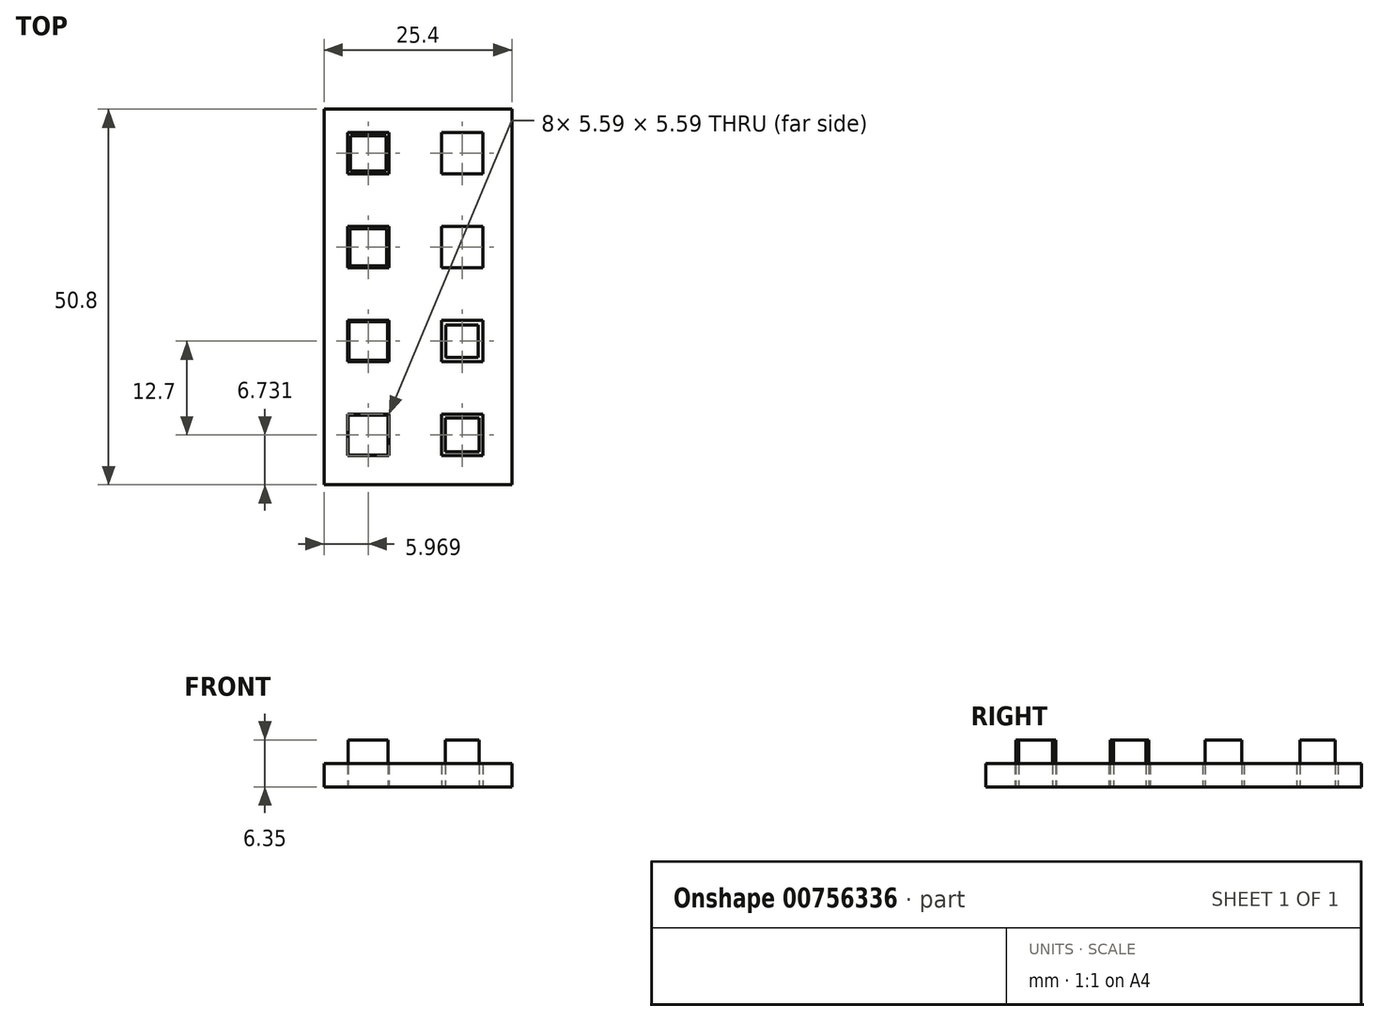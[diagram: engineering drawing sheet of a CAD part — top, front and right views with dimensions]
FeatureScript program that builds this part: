
annotation { "Feature Type Name" : "Feature", "Feature Type Description" : "" }
export const myFeature = defineFeature(function(context is Context, id is Id, definition is map)
    precondition{}
    {
        {
            var Q0;
            Q0=qCreatedBy(makeId("Top.planeOp"),FACE);
            var sketch = newSketch(context, id + "F0", { "sketchPlane" : qUnion([Q0])});
            skLineSegment(sketch, "E0.bottom", {"start": v(0, 0) * mm, "end": v(50.8, 0) * mm});
            skLineSegment(sketch, "E0.top", {"start": v(0, 50.8) * mm, "end": v(50.8, 50.8) * mm});
            skLineSegment(sketch, "E0.left", {"start": v(0, 0) * mm, "end": v(0, 50.8) * mm});
            skLineSegment(sketch, "E0.right", {"start": v(50.8, 0) * mm, "end": v(50.8, 50.8) * mm});
            skLineSegment(sketch, "E1.bottom", {"start": v(3.17, 47.63) * mm, "end": v(8.76, 47.63) * mm});
            skLineSegment(sketch, "E1.top", {"start": v(3.17, 42.04) * mm, "end": v(8.76, 42.04) * mm});
            skLineSegment(sketch, "E1.left", {"start": v(3.17, 47.63) * mm, "end": v(3.17, 42.04) * mm});
            skLineSegment(sketch, "E1.right", {"start": v(8.76, 47.63) * mm, "end": v(8.76, 42.04) * mm});
            skLineSegment(sketch, "E2.0.1.0", {"start": v(3.17, 34.93) * mm, "end": v(8.76, 34.93) * mm});
            skLineSegment(sketch, "E2.0.1.1", {"start": v(3.17, 29.34) * mm, "end": v(8.76, 29.34) * mm});
            skLineSegment(sketch, "E2.0.1.2", {"start": v(8.76, 34.93) * mm, "end": v(8.76, 29.34) * mm});
            skLineSegment(sketch, "E2.0.1.3", {"start": v(3.17, 34.93) * mm, "end": v(3.17, 29.34) * mm});
            skLineSegment(sketch, "E2.0.2.0", {"start": v(3.17, 22.23) * mm, "end": v(8.76, 22.23) * mm});
            skLineSegment(sketch, "E2.0.2.1", {"start": v(3.18, 16.64) * mm, "end": v(8.76, 16.64) * mm});
            skLineSegment(sketch, "E2.0.2.2", {"start": v(8.76, 22.23) * mm, "end": v(8.76, 16.64) * mm});
            skLineSegment(sketch, "E2.0.2.3", {"start": v(3.17, 22.23) * mm, "end": v(3.17, 16.64) * mm});
            skLineSegment(sketch, "E2.0.3.0", {"start": v(3.17, 9.53) * mm, "end": v(8.76, 9.53) * mm});
            skLineSegment(sketch, "E2.0.3.1", {"start": v(3.18, 3.94) * mm, "end": v(8.76, 3.94) * mm});
            skLineSegment(sketch, "E2.0.3.2", {"start": v(8.76, 9.53) * mm, "end": v(8.76, 3.94) * mm});
            skLineSegment(sketch, "E2.0.3.3", {"start": v(3.17, 9.53) * mm, "end": v(3.17, 3.94) * mm});
            skLineSegment(sketch, "E2.1.0.0", {"start": v(15.87, 47.63) * mm, "end": v(21.46, 47.63) * mm});
            skLineSegment(sketch, "E2.1.0.1", {"start": v(15.87, 42.04) * mm, "end": v(21.46, 42.04) * mm});
            skLineSegment(sketch, "E2.1.0.2", {"start": v(21.46, 47.63) * mm, "end": v(21.46, 42.04) * mm});
            skLineSegment(sketch, "E2.1.0.3", {"start": v(15.87, 47.63) * mm, "end": v(15.87, 42.04) * mm});
            skLineSegment(sketch, "E2.1.1.0", {"start": v(15.87, 34.93) * mm, "end": v(21.46, 34.93) * mm});
            skLineSegment(sketch, "E2.1.1.1", {"start": v(15.88, 29.34) * mm, "end": v(21.46, 29.34) * mm});
            skLineSegment(sketch, "E2.1.1.2", {"start": v(21.46, 34.93) * mm, "end": v(21.46, 29.34) * mm});
            skLineSegment(sketch, "E2.1.1.3", {"start": v(15.87, 34.93) * mm, "end": v(15.87, 29.34) * mm});
            skLineSegment(sketch, "E2.1.2.0", {"start": v(15.87, 22.23) * mm, "end": v(21.46, 22.23) * mm});
            skLineSegment(sketch, "E2.1.2.1", {"start": v(15.88, 16.64) * mm, "end": v(21.46, 16.64) * mm});
            skLineSegment(sketch, "E2.1.2.2", {"start": v(21.46, 22.23) * mm, "end": v(21.46, 16.64) * mm});
            skLineSegment(sketch, "E2.1.2.3", {"start": v(15.87, 22.23) * mm, "end": v(15.87, 16.64) * mm});
            skLineSegment(sketch, "E2.1.3.0", {"start": v(15.87, 9.53) * mm, "end": v(21.46, 9.53) * mm});
            skLineSegment(sketch, "E2.1.3.1", {"start": v(15.88, 3.94) * mm, "end": v(21.46, 3.94) * mm});
            skLineSegment(sketch, "E2.1.3.2", {"start": v(21.46, 9.53) * mm, "end": v(21.46, 3.94) * mm});
            skLineSegment(sketch, "E2.1.3.3", {"start": v(15.87, 9.53) * mm, "end": v(15.87, 3.94) * mm});
            skLineSegment(sketch, "E2.2.0.0", {"start": v(28.57, 47.63) * mm, "end": v(34.16, 47.63) * mm});
            skLineSegment(sketch, "E2.2.0.1", {"start": v(28.57, 42.04) * mm, "end": v(34.16, 42.04) * mm});
            skLineSegment(sketch, "E2.2.0.2", {"start": v(34.16, 47.63) * mm, "end": v(34.16, 42.04) * mm});
            skLineSegment(sketch, "E2.2.0.3", {"start": v(28.57, 47.63) * mm, "end": v(28.57, 42.04) * mm});
            skLineSegment(sketch, "E2.2.1.0", {"start": v(28.57, 34.93) * mm, "end": v(34.16, 34.93) * mm});
            skLineSegment(sketch, "E2.2.1.1", {"start": v(28.57, 29.34) * mm, "end": v(34.16, 29.34) * mm});
            skLineSegment(sketch, "E2.2.1.2", {"start": v(34.16, 34.93) * mm, "end": v(34.16, 29.34) * mm});
            skLineSegment(sketch, "E2.2.1.3", {"start": v(28.57, 34.93) * mm, "end": v(28.57, 29.34) * mm});
            skLineSegment(sketch, "E2.2.2.0", {"start": v(28.57, 22.23) * mm, "end": v(34.16, 22.23) * mm});
            skLineSegment(sketch, "E2.2.2.1", {"start": v(28.57, 16.64) * mm, "end": v(34.16, 16.64) * mm});
            skLineSegment(sketch, "E2.2.2.2", {"start": v(34.16, 22.23) * mm, "end": v(34.16, 16.64) * mm});
            skLineSegment(sketch, "E2.2.2.3", {"start": v(28.57, 22.23) * mm, "end": v(28.57, 16.64) * mm});
            skLineSegment(sketch, "E2.2.3.0", {"start": v(28.57, 9.53) * mm, "end": v(34.16, 9.53) * mm});
            skLineSegment(sketch, "E2.2.3.1", {"start": v(28.58, 3.94) * mm, "end": v(34.16, 3.94) * mm});
            skLineSegment(sketch, "E2.2.3.2", {"start": v(34.16, 9.53) * mm, "end": v(34.16, 3.94) * mm});
            skLineSegment(sketch, "E2.2.3.3", {"start": v(28.57, 9.53) * mm, "end": v(28.57, 3.94) * mm});
            skLineSegment(sketch, "E2.3.0.0", {"start": v(41.27, 47.63) * mm, "end": v(46.86, 47.63) * mm});
            skLineSegment(sketch, "E2.3.0.1", {"start": v(41.27, 42.04) * mm, "end": v(46.86, 42.04) * mm});
            skLineSegment(sketch, "E2.3.0.2", {"start": v(46.86, 47.63) * mm, "end": v(46.86, 42.04) * mm});
            skLineSegment(sketch, "E2.3.0.3", {"start": v(41.28, 47.63) * mm, "end": v(41.28, 42.04) * mm});
            skLineSegment(sketch, "E2.3.1.0", {"start": v(41.27, 34.93) * mm, "end": v(46.86, 34.93) * mm});
            skLineSegment(sketch, "E2.3.1.1", {"start": v(41.27, 29.34) * mm, "end": v(46.86, 29.34) * mm});
            skLineSegment(sketch, "E2.3.1.2", {"start": v(46.86, 34.93) * mm, "end": v(46.86, 29.34) * mm});
            skLineSegment(sketch, "E2.3.1.3", {"start": v(41.28, 34.93) * mm, "end": v(41.28, 29.34) * mm});
            skLineSegment(sketch, "E2.3.2.0", {"start": v(41.27, 22.23) * mm, "end": v(46.86, 22.23) * mm});
            skLineSegment(sketch, "E2.3.2.1", {"start": v(41.27, 16.64) * mm, "end": v(46.86, 16.64) * mm});
            skLineSegment(sketch, "E2.3.2.2", {"start": v(46.86, 22.23) * mm, "end": v(46.86, 16.64) * mm});
            skLineSegment(sketch, "E2.3.2.3", {"start": v(41.28, 22.23) * mm, "end": v(41.28, 16.64) * mm});
            skLineSegment(sketch, "E2.3.3.0", {"start": v(41.27, 9.53) * mm, "end": v(46.86, 9.53) * mm});
            skLineSegment(sketch, "E2.3.3.1", {"start": v(41.27, 3.94) * mm, "end": v(46.86, 3.94) * mm});
            skLineSegment(sketch, "E2.3.3.2", {"start": v(46.86, 9.53) * mm, "end": v(46.86, 3.94) * mm});
            skLineSegment(sketch, "E2.3.3.3", {"start": v(41.28, 9.53) * mm, "end": v(41.28, 3.94) * mm});
            skLineSegment(sketch, "E2.direction1", {"start": v(3.17, 42.04) * mm, "end": v(15.87, 42.04) * mm, "construction": true});
            skLineSegment(sketch, "E2.direction2", {"start": v(3.17, 42.04) * mm, "end": v(3.17, 29.34) * mm, "construction": true});
            skSolve(sketch);
        }
        {
            var Q0;
            Q0 = qSketchRegion(id + "F0", true);
            extrude(context, id + "F1", {"entities" : qUnion([Q0]), "depth" : 3.17 * mm, "offsetDistance" : 25.4 * mm});
        }
        {
            var Q0;
            Q0=makeQuery(id+"F1.opExtrude","CAP_FACE",FACE,{"disambiguationData":[OSD([sQuery(id+"F0.wireOp",EDGE,"E0.bottom"),sQuery(id+"F0.wireOp",EDGE,"E0.top"),sQuery(id+"F0.wireOp",EDGE,"E0.left"),sQuery(id+"F0.wireOp",EDGE,"E0.right"),sQuery(id+"F0.wireOp",EDGE,"E1.bottom"),sQuery(id+"F0.wireOp",EDGE,"E1.top"),sQuery(id+"F0.wireOp",EDGE,"E1.left"),sQuery(id+"F0.wireOp",EDGE,"E1.right"),sQuery(id+"F0.wireOp",EDGE,"E2.0.1.0"),sQuery(id+"F0.wireOp",EDGE,"E2.0.1.1"),sQuery(id+"F0.wireOp",EDGE,"E2.0.1.2"),sQuery(id+"F0.wireOp",EDGE,"E2.0.1.3"),sQuery(id+"F0.wireOp",EDGE,"E2.0.2.0"),sQuery(id+"F0.wireOp",EDGE,"E2.0.2.1"),sQuery(id+"F0.wireOp",EDGE,"E2.0.2.2"),sQuery(id+"F0.wireOp",EDGE,"E2.0.2.3"),sQuery(id+"F0.wireOp",EDGE,"E2.0.3.0"),sQuery(id+"F0.wireOp",EDGE,"E2.0.3.1"),sQuery(id+"F0.wireOp",EDGE,"E2.0.3.2"),sQuery(id+"F0.wireOp",EDGE,"E2.0.3.3"),sQuery(id+"F0.wireOp",EDGE,"E2.1.0.0"),sQuery(id+"F0.wireOp",EDGE,"E2.1.0.1"),sQuery(id+"F0.wireOp",EDGE,"E2.1.0.2"),sQuery(id+"F0.wireOp",EDGE,"E2.1.0.3"),sQuery(id+"F0.wireOp",EDGE,"E2.1.1.0"),sQuery(id+"F0.wireOp",EDGE,"E2.1.1.1"),sQuery(id+"F0.wireOp",EDGE,"E2.1.1.2"),sQuery(id+"F0.wireOp",EDGE,"E2.1.1.3"),sQuery(id+"F0.wireOp",EDGE,"E2.1.2.0"),sQuery(id+"F0.wireOp",EDGE,"E2.1.2.1"),sQuery(id+"F0.wireOp",EDGE,"E2.1.2.2"),sQuery(id+"F0.wireOp",EDGE,"E2.1.2.3"),sQuery(id+"F0.wireOp",EDGE,"E2.1.3.0"),sQuery(id+"F0.wireOp",EDGE,"E2.1.3.1"),sQuery(id+"F0.wireOp",EDGE,"E2.1.3.2"),sQuery(id+"F0.wireOp",EDGE,"E2.1.3.3"),sQuery(id+"F0.wireOp",EDGE,"E2.2.0.0"),sQuery(id+"F0.wireOp",EDGE,"E2.2.0.1"),sQuery(id+"F0.wireOp",EDGE,"E2.2.0.2"),sQuery(id+"F0.wireOp",EDGE,"E2.2.0.3"),sQuery(id+"F0.wireOp",EDGE,"E2.2.1.0"),sQuery(id+"F0.wireOp",EDGE,"E2.2.1.1"),sQuery(id+"F0.wireOp",EDGE,"E2.2.1.2"),sQuery(id+"F0.wireOp",EDGE,"E2.2.1.3"),sQuery(id+"F0.wireOp",EDGE,"E2.2.2.0"),sQuery(id+"F0.wireOp",EDGE,"E2.2.2.1"),sQuery(id+"F0.wireOp",EDGE,"E2.2.2.2"),sQuery(id+"F0.wireOp",EDGE,"E2.2.2.3"),sQuery(id+"F0.wireOp",EDGE,"E2.2.3.0"),sQuery(id+"F0.wireOp",EDGE,"E2.2.3.1"),sQuery(id+"F0.wireOp",EDGE,"E2.2.3.2"),sQuery(id+"F0.wireOp",EDGE,"E2.2.3.3"),sQuery(id+"F0.wireOp",EDGE,"E2.3.0.0"),sQuery(id+"F0.wireOp",EDGE,"E2.3.0.1"),sQuery(id+"F0.wireOp",EDGE,"E2.3.0.2"),sQuery(id+"F0.wireOp",EDGE,"E2.3.0.3"),sQuery(id+"F0.wireOp",EDGE,"E2.3.1.0"),sQuery(id+"F0.wireOp",EDGE,"E2.3.1.1"),sQuery(id+"F0.wireOp",EDGE,"E2.3.1.2"),sQuery(id+"F0.wireOp",EDGE,"E2.3.1.3"),sQuery(id+"F0.wireOp",EDGE,"E2.3.2.0"),sQuery(id+"F0.wireOp",EDGE,"E2.3.2.1"),sQuery(id+"F0.wireOp",EDGE,"E2.3.2.2"),sQuery(id+"F0.wireOp",EDGE,"E2.3.2.3"),sQuery(id+"F0.wireOp",EDGE,"E2.3.3.0"),sQuery(id+"F0.wireOp",EDGE,"E2.3.3.1"),sQuery(id+"F0.wireOp",EDGE,"E2.3.3.2"),sQuery(id+"F0.wireOp",EDGE,"E2.3.3.3")])],"isStart":false});
            var sketch = newSketch(context, id + "F2", { "sketchPlane" : qUnion([Q0])});
            skLineSegment(sketch, "E3.0", {"start": v(3.27, 9.43) * mm, "end": v(3.27, 4.04) * mm});
            skLineSegment(sketch, "E3.1", {"start": v(3.27, 9.43) * mm, "end": v(8.66, 9.43) * mm});
            skLineSegment(sketch, "E3.2", {"start": v(8.66, 9.43) * mm, "end": v(8.66, 4.04) * mm});
            skLineSegment(sketch, "E3.3", {"start": v(3.27, 4.04) * mm, "end": v(8.66, 4.04) * mm});
            skLineSegment(sketch, "E4.0", {"start": v(3.37, 22.03) * mm, "end": v(3.37, 16.84) * mm});
            skLineSegment(sketch, "E4.1", {"start": v(3.37, 22.03) * mm, "end": v(8.56, 22.03) * mm});
            skLineSegment(sketch, "E4.2", {"start": v(8.56, 22.03) * mm, "end": v(8.56, 16.84) * mm});
            skLineSegment(sketch, "E4.3", {"start": v(3.37, 16.84) * mm, "end": v(8.56, 16.84) * mm});
            skLineSegment(sketch, "E5.0", {"start": v(3.47, 34.63) * mm, "end": v(3.47, 29.64) * mm});
            skLineSegment(sketch, "E5.1", {"start": v(3.47, 34.63) * mm, "end": v(8.46, 34.63) * mm});
            skLineSegment(sketch, "E5.2", {"start": v(8.46, 34.63) * mm, "end": v(8.46, 29.64) * mm});
            skLineSegment(sketch, "E5.3", {"start": v(3.47, 29.64) * mm, "end": v(8.46, 29.64) * mm});
            skLineSegment(sketch, "E6.0", {"start": v(3.57, 47.23) * mm, "end": v(3.57, 42.44) * mm});
            skLineSegment(sketch, "E6.1", {"start": v(3.57, 47.23) * mm, "end": v(8.36, 47.23) * mm});
            skLineSegment(sketch, "E6.2", {"start": v(8.36, 47.23) * mm, "end": v(8.36, 42.44) * mm});
            skLineSegment(sketch, "E6.3", {"start": v(3.57, 42.44) * mm, "end": v(8.36, 42.44) * mm});
            skLineSegment(sketch, "E7.0", {"start": v(16.37, 9.03) * mm, "end": v(16.37, 4.44) * mm});
            skLineSegment(sketch, "E7.1", {"start": v(16.37, 9.03) * mm, "end": v(20.96, 9.03) * mm});
            skLineSegment(sketch, "E7.2", {"start": v(20.96, 9.03) * mm, "end": v(20.96, 4.44) * mm});
            skLineSegment(sketch, "E7.3", {"start": v(16.37, 4.44) * mm, "end": v(20.96, 4.44) * mm});
            skLineSegment(sketch, "E8.0", {"start": v(16.47, 21.63) * mm, "end": v(16.47, 17.24) * mm});
            skLineSegment(sketch, "E8.1", {"start": v(16.47, 21.63) * mm, "end": v(20.86, 21.63) * mm});
            skLineSegment(sketch, "E8.2", {"start": v(20.86, 21.63) * mm, "end": v(20.86, 17.24) * mm});
            skLineSegment(sketch, "E8.3", {"start": v(16.47, 17.24) * mm, "end": v(20.86, 17.24) * mm});
            skSolve(sketch);
        }
        {
            var Q0;
            Q0=makeQuery(id+"F2.imprint","IMPRINT",FACE,{"disambiguationData":[TD([[makeQuery(id+"F2.imprint","IMPRINT",EDGE,{"derivedFrom":sQuery(id+"F2.wireOp",EDGE,"E4.0")}),1.0]])]});
            var Q1;
            Q1=makeQuery(id+"F2.imprint","IMPRINT",FACE,{"disambiguationData":[TD([[makeQuery(id+"F2.imprint","IMPRINT",EDGE,{"derivedFrom":sQuery(id+"F2.wireOp",EDGE,"E3.0")}),1.0]])]});
            var Q2;
            Q2=makeQuery(id+"F2.imprint","IMPRINT",FACE,{"disambiguationData":[TD([[makeQuery(id+"F2.imprint","IMPRINT",EDGE,{"derivedFrom":sQuery(id+"F2.wireOp",EDGE,"E5.0")}),1.0]])]});
            var Q3;
            Q3=makeQuery(id+"F2.imprint","IMPRINT",FACE,{"disambiguationData":[TD([[makeQuery(id+"F2.imprint","IMPRINT",EDGE,{"derivedFrom":sQuery(id+"F2.wireOp",EDGE,"E6.0")}),1.0]])]});
            var Q4;
            Q4=makeQuery(id+"F2.imprint","IMPRINT",FACE,{"disambiguationData":[TD([[makeQuery(id+"F2.imprint","IMPRINT",EDGE,{"derivedFrom":sQuery(id+"F2.wireOp",EDGE,"E8.0")}),1.0]])]});
            var Q5;
            Q5=makeQuery(id+"F2.imprint","IMPRINT",FACE,{"disambiguationData":[TD([[makeQuery(id+"F2.imprint","IMPRINT",EDGE,{"derivedFrom":sQuery(id+"F2.wireOp",EDGE,"E7.0")}),1.0]])]});
            extrude(context, id + "F3", {"entities" : qUnion([Q0, Q1, Q2, Q3, Q4, Q5]), "depth" : 3.17 * mm, "offsetDistance" : 25.4 * mm, "hasSecondDirection" : true, "secondDirectionOppositeDirection" : true, "secondDirectionDepth" : 3.17 * mm});
        }
        {
            var Q0;
            Q0=makeQuery(id+"F1.opExtrude","CAP_FACE",FACE,{"disambiguationData":[OSD([sQuery(id+"F0.wireOp",EDGE,"E0.bottom"),sQuery(id+"F0.wireOp",EDGE,"E0.top"),sQuery(id+"F0.wireOp",EDGE,"E0.left"),sQuery(id+"F0.wireOp",EDGE,"E0.right"),sQuery(id+"F0.wireOp",EDGE,"E1.bottom"),sQuery(id+"F0.wireOp",EDGE,"E1.top"),sQuery(id+"F0.wireOp",EDGE,"E1.left"),sQuery(id+"F0.wireOp",EDGE,"E1.right"),sQuery(id+"F0.wireOp",EDGE,"E2.0.1.0"),sQuery(id+"F0.wireOp",EDGE,"E2.0.1.1"),sQuery(id+"F0.wireOp",EDGE,"E2.0.1.2"),sQuery(id+"F0.wireOp",EDGE,"E2.0.1.3"),sQuery(id+"F0.wireOp",EDGE,"E2.0.2.0"),sQuery(id+"F0.wireOp",EDGE,"E2.0.2.1"),sQuery(id+"F0.wireOp",EDGE,"E2.0.2.2"),sQuery(id+"F0.wireOp",EDGE,"E2.0.2.3"),sQuery(id+"F0.wireOp",EDGE,"E2.0.3.0"),sQuery(id+"F0.wireOp",EDGE,"E2.0.3.1"),sQuery(id+"F0.wireOp",EDGE,"E2.0.3.2"),sQuery(id+"F0.wireOp",EDGE,"E2.0.3.3"),sQuery(id+"F0.wireOp",EDGE,"E2.1.0.0"),sQuery(id+"F0.wireOp",EDGE,"E2.1.0.1"),sQuery(id+"F0.wireOp",EDGE,"E2.1.0.2"),sQuery(id+"F0.wireOp",EDGE,"E2.1.0.3"),sQuery(id+"F0.wireOp",EDGE,"E2.1.1.0"),sQuery(id+"F0.wireOp",EDGE,"E2.1.1.1"),sQuery(id+"F0.wireOp",EDGE,"E2.1.1.2"),sQuery(id+"F0.wireOp",EDGE,"E2.1.1.3"),sQuery(id+"F0.wireOp",EDGE,"E2.1.2.0"),sQuery(id+"F0.wireOp",EDGE,"E2.1.2.1"),sQuery(id+"F0.wireOp",EDGE,"E2.1.2.2"),sQuery(id+"F0.wireOp",EDGE,"E2.1.2.3"),sQuery(id+"F0.wireOp",EDGE,"E2.1.3.0"),sQuery(id+"F0.wireOp",EDGE,"E2.1.3.1"),sQuery(id+"F0.wireOp",EDGE,"E2.1.3.2"),sQuery(id+"F0.wireOp",EDGE,"E2.1.3.3"),sQuery(id+"F0.wireOp",EDGE,"E2.2.0.0"),sQuery(id+"F0.wireOp",EDGE,"E2.2.0.1"),sQuery(id+"F0.wireOp",EDGE,"E2.2.0.2"),sQuery(id+"F0.wireOp",EDGE,"E2.2.0.3"),sQuery(id+"F0.wireOp",EDGE,"E2.2.1.0"),sQuery(id+"F0.wireOp",EDGE,"E2.2.1.1"),sQuery(id+"F0.wireOp",EDGE,"E2.2.1.2"),sQuery(id+"F0.wireOp",EDGE,"E2.2.1.3"),sQuery(id+"F0.wireOp",EDGE,"E2.2.2.0"),sQuery(id+"F0.wireOp",EDGE,"E2.2.2.1"),sQuery(id+"F0.wireOp",EDGE,"E2.2.2.2"),sQuery(id+"F0.wireOp",EDGE,"E2.2.2.3"),sQuery(id+"F0.wireOp",EDGE,"E2.2.3.0"),sQuery(id+"F0.wireOp",EDGE,"E2.2.3.1"),sQuery(id+"F0.wireOp",EDGE,"E2.2.3.2"),sQuery(id+"F0.wireOp",EDGE,"E2.2.3.3"),sQuery(id+"F0.wireOp",EDGE,"E2.3.0.0"),sQuery(id+"F0.wireOp",EDGE,"E2.3.0.1"),sQuery(id+"F0.wireOp",EDGE,"E2.3.0.2"),sQuery(id+"F0.wireOp",EDGE,"E2.3.0.3"),sQuery(id+"F0.wireOp",EDGE,"E2.3.1.0"),sQuery(id+"F0.wireOp",EDGE,"E2.3.1.1"),sQuery(id+"F0.wireOp",EDGE,"E2.3.1.2"),sQuery(id+"F0.wireOp",EDGE,"E2.3.1.3"),sQuery(id+"F0.wireOp",EDGE,"E2.3.2.0"),sQuery(id+"F0.wireOp",EDGE,"E2.3.2.1"),sQuery(id+"F0.wireOp",EDGE,"E2.3.2.2"),sQuery(id+"F0.wireOp",EDGE,"E2.3.2.3"),sQuery(id+"F0.wireOp",EDGE,"E2.3.3.0"),sQuery(id+"F0.wireOp",EDGE,"E2.3.3.1"),sQuery(id+"F0.wireOp",EDGE,"E2.3.3.2"),sQuery(id+"F0.wireOp",EDGE,"E2.3.3.3")])],"isStart":false});
            var sketch = newSketch(context, id + "F4", { "sketchPlane" : qUnion([Q0])});
            skLineSegment(sketch, "E9", {"start": v(25.4, 0) * mm, "end": v(25.4, 50.8) * mm});
            skLineSegment(sketch, "E10", {"start": v(25.4, 25.4) * mm, "end": v(12.05, 25.4) * mm});
            skLineSegment(sketch, "E11", {"start": v(12.05, 25.48) * mm, "end": v(12.05, 50.8) * mm});
            skLineSegment(sketch, "E12", {"start": v(12.05, 50.8) * mm, "end": v(50.8, 50.8) * mm});
            skLineSegment(sketch, "E13", {"start": v(50.8, 50.8) * mm, "end": v(50.8, 0) * mm});
            skLineSegment(sketch, "E14", {"start": v(50.8, 0) * mm, "end": v(25.4, 0) * mm});
            skSolve(sketch);
        }
        {
            var Q0;
            Q0 = qSketchRegion(id + "F4", true);
            extrude(context, id + "F5", {"entities" : qUnion([Q0]), "operationType" : NewBodyOperationType.REMOVE, "oppositeDirection" : true, "depth" : 25.4 * mm, "offsetDistance" : 25.4 * mm});
        }
    });
